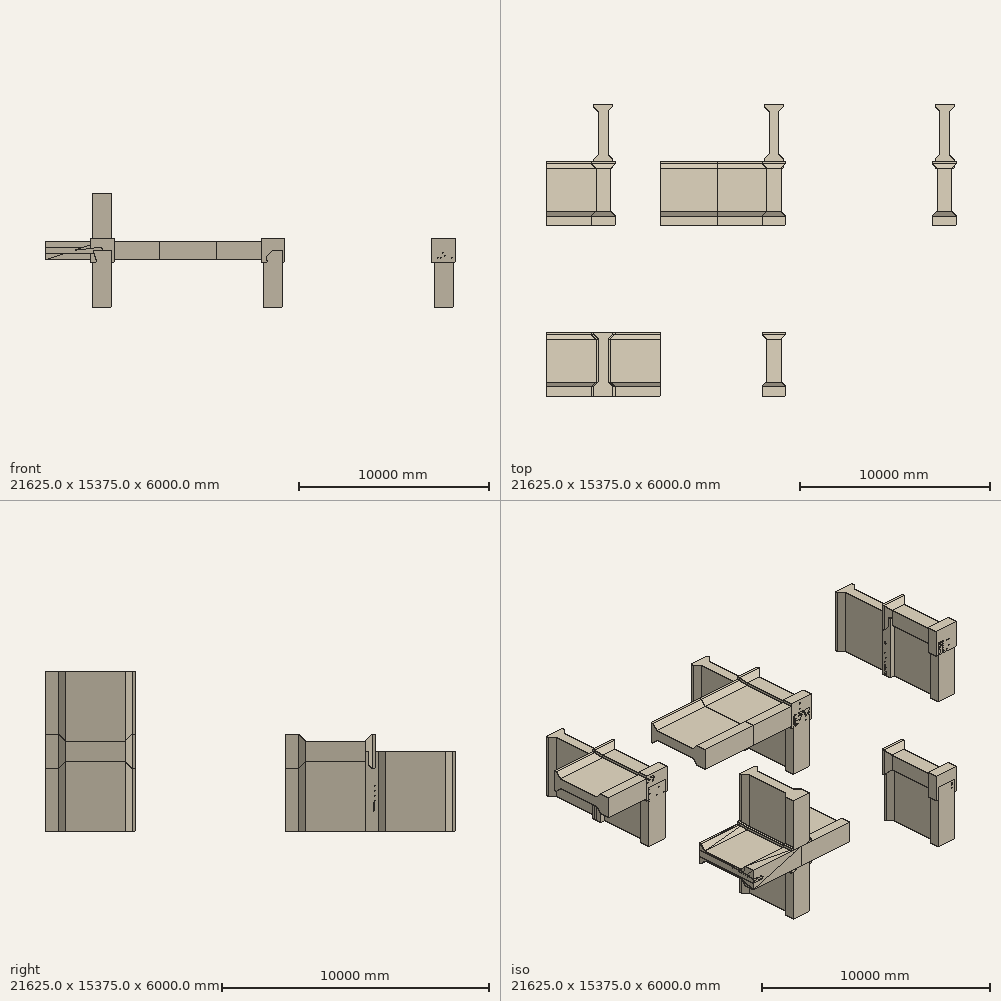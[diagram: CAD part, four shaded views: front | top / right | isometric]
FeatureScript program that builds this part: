
annotation { "Feature Type Name" : "Feature", "Feature Type Description" : "" }
export const myFeature = defineFeature(function(context is Context, id is Id, definition is map)
    precondition{}
    {
        {
            var Q0;
            Q0=qCreatedBy(makeId("Top.planeOp"),FACE);
            var sketch = newSketch(context, id + "F0", { "sketchPlane" : qUnion([Q0])});
            skLineSegment(sketch, "E0", {"start": v(-500, 0) * mm, "end": v(500, 0) * mm});
            skLineSegment(sketch, "E1", {"start": v(500, 0) * mm, "end": v(500, 500) * mm});
            skLineSegment(sketch, "E2", {"start": v(500, 500) * mm, "end": v(250, 750) * mm});
            skLineSegment(sketch, "E3", {"start": v(250, 750) * mm, "end": v(250, 3000) * mm});
            skLineSegment(sketch, "E4", {"start": v(500, 500) * mm, "end": v(250, 500) * mm, "construction": true});
            skLineSegment(sketch, "E5", {"start": v(0, 0) * mm, "end": v(0, 3375) * mm, "construction": true});
            skLineSegment(sketch, "E6", {"start": v(250, 3000) * mm, "end": v(500, 3250) * mm});
            skLineSegment(sketch, "E7", {"start": v(500, 3250) * mm, "end": v(500, 3375) * mm});
            skLineSegment(sketch, "E8", {"start": v(500, 3375) * mm, "end": v(-500, 3375) * mm});
            skLineSegment(sketch, "E9.MirrorCS", {"start": v(-500, 0) * mm, "end": v(-500, 500) * mm});
            skLineSegment(sketch, "E10.MirrorCS", {"start": v(-500, 500) * mm, "end": v(-250, 750) * mm});
            skLineSegment(sketch, "E11.MirrorCS", {"start": v(-250, 750) * mm, "end": v(-250, 3000) * mm});
            skLineSegment(sketch, "E12.MirrorCS", {"start": v(-250, 3000) * mm, "end": v(-500, 3250) * mm});
            skLineSegment(sketch, "E13.MirrorCS", {"start": v(-500, 3250) * mm, "end": v(-500, 3375) * mm});
            skLineSegment(sketch, "E14", {"start": v(-625, 0) * mm, "end": v(625, 0) * mm});
            skLineSegment(sketch, "E15", {"start": v(625, 0) * mm, "end": v(625, 500) * mm});
            skLineSegment(sketch, "E16", {"start": v(625, 500) * mm, "end": v(375, 750) * mm});
            skLineSegment(sketch, "E17", {"start": v(375, 750) * mm, "end": v(375, 3000) * mm});
            skLineSegment(sketch, "E18", {"start": v(375, 3000) * mm, "end": v(625, 3250) * mm});
            skLineSegment(sketch, "E19", {"start": v(625, 3250) * mm, "end": v(625, 3375) * mm});
            skLineSegment(sketch, "E20", {"start": v(625, 3375) * mm, "end": v(-625, 3375) * mm});
            skLineSegment(sketch, "E21.MirrorCS", {"start": v(-625, 0) * mm, "end": v(-625, 500) * mm});
            skLineSegment(sketch, "E22.MirrorCS", {"start": v(-625, 500) * mm, "end": v(-375, 750) * mm});
            skLineSegment(sketch, "E23.MirrorCS", {"start": v(-375, 750) * mm, "end": v(-375, 3000) * mm});
            skLineSegment(sketch, "E24.MirrorCS", {"start": v(-375, 3000) * mm, "end": v(-625, 3250) * mm});
            skLineSegment(sketch, "E25.MirrorCS", {"start": v(-625, 3250) * mm, "end": v(-625, 3375) * mm});
            skLineSegment(sketch, "E26", {"start": v(-625, 500) * mm, "end": v(625, 500) * mm});
            skLineSegment(sketch, "E27", {"start": v(375, 750) * mm, "end": v(-375, 750) * mm});
            skLineSegment(sketch, "E28", {"start": v(-375, 3000) * mm, "end": v(375, 3000) * mm});
            skLineSegment(sketch, "E29", {"start": v(-625, 3250) * mm, "end": v(625, 3250) * mm});
            skCircle(sketch, "E30", {"center": v(1625, 1250) * mm, "radius": 1250 * mm, "construction": true});
            skSolve(sketch);
        }
        {
            var Q0;
            {var subQ0=sQuery(id+"F0.wireOp",EDGE,"E11.MirrorCS");Q0=makeQuery(id+"F0.imprint","IMPRINT",FACE,{"disambiguationData":[TD([[makeQuery(id+"F0.imprint","IMPRINT",EDGE,{"derivedFrom":subQ0}),1.0]])]});}
            var Q1;
            {var subQ0=sQuery(id+"F0.wireOp",EDGE,"E3");Q1=makeQuery(id+"F0.imprint","IMPRINT",FACE,{"disambiguationData":[TD([[makeQuery(id+"F0.imprint","IMPRINT",EDGE,{"derivedFrom":subQ0}),-1.0]])]});}
            var Q2;
            {var subQ0=sQuery(id+"F0.wireOp",EDGE,"E3");Q2=makeQuery(id+"F0.imprint","IMPRINT",FACE,{"disambiguationData":[TD([[makeQuery(id+"F0.imprint","IMPRINT",EDGE,{"derivedFrom":subQ0}),1.0]])]});}
            extrude(context, id + "F1", {"entities" : qUnion([Q0, Q1, Q2]), "endBound" : BoundingType.SYMMETRIC, "depth" : 750 * mm, "offsetDistance" : 25 * mm});
        }
        {
            var Q0;
            {var subQ0=sQuery(id+"F0.wireOp",EDGE,"E1");Q0=makeQuery(id+"F0.imprint","IMPRINT",FACE,{"disambiguationData":[TD([[makeQuery(id+"F0.imprint","IMPRINT",EDGE,{"derivedFrom":subQ0}),-1.0]])]});}
            var Q1;
            {var subQ0=sQuery(id+"F0.wireOp",EDGE,"E2");Q1=makeQuery(id+"F0.imprint","IMPRINT",FACE,{"disambiguationData":[TD([[makeQuery(id+"F0.imprint","IMPRINT",EDGE,{"derivedFrom":subQ0}),-1.0]])]});}
            var Q2;
            {var subQ0=sQuery(id+"F0.wireOp",EDGE,"E6");Q2=makeQuery(id+"F0.imprint","IMPRINT",FACE,{"disambiguationData":[TD([[makeQuery(id+"F0.imprint","IMPRINT",EDGE,{"derivedFrom":subQ0}),-1.0]])]});}
            var Q3;
            {var subQ0=sQuery(id+"F0.wireOp",EDGE,"E7");Q3=makeQuery(id+"F0.imprint","IMPRINT",FACE,{"disambiguationData":[TD([[makeQuery(id+"F0.imprint","IMPRINT",EDGE,{"derivedFrom":subQ0}),-1.0]])]});}
            var Q4;
            {var subQ0=sQuery(id+"F0.wireOp",EDGE,"E9.MirrorCS");Q4=makeQuery(id+"F0.imprint","IMPRINT",FACE,{"disambiguationData":[TD([[makeQuery(id+"F0.imprint","IMPRINT",EDGE,{"derivedFrom":subQ0}),1.0]])]});}
            var Q5;
            {var subQ0=sQuery(id+"F0.wireOp",EDGE,"E10.MirrorCS");Q5=makeQuery(id+"F0.imprint","IMPRINT",FACE,{"disambiguationData":[TD([[makeQuery(id+"F0.imprint","IMPRINT",EDGE,{"derivedFrom":subQ0}),1.0]])]});}
            var Q6;
            {var subQ0=sQuery(id+"F0.wireOp",EDGE,"E12.MirrorCS");Q6=makeQuery(id+"F0.imprint","IMPRINT",FACE,{"disambiguationData":[TD([[makeQuery(id+"F0.imprint","IMPRINT",EDGE,{"derivedFrom":subQ0}),1.0]])]});}
            var Q7;
            {var subQ0=sQuery(id+"F0.wireOp",EDGE,"E13.MirrorCS");Q7=makeQuery(id+"F0.imprint","IMPRINT",FACE,{"disambiguationData":[TD([[makeQuery(id+"F0.imprint","IMPRINT",EDGE,{"derivedFrom":subQ0}),1.0]])]});}
            var Q8;
            {var subQ0=sQuery(id+"F0.wireOp",EDGE,"E7");Q8=makeQuery(id+"F0.imprint","IMPRINT",FACE,{"disambiguationData":[TD([[makeQuery(id+"F0.imprint","IMPRINT",EDGE,{"derivedFrom":subQ0}),1.0]])]});}
            var Q9;
            Q9=makeQuery(id+"F0.imprint","IMPRINT",FACE,{"disambiguationData":[TD([[makeQuery(id+"F0.imprint","IMPRINT",EDGE,{"derivedFrom":sQuery(id+"F0.wireOp",EDGE,"E0")}),1.0]])]});
            var Q10;
            {var subQ0=sQuery(id+"F0.wireOp",EDGE,"E2");Q10=makeQuery(id+"F0.imprint","IMPRINT",FACE,{"disambiguationData":[TD([[makeQuery(id+"F0.imprint","IMPRINT",EDGE,{"derivedFrom":subQ0}),1.0]])]});}
            var Q11;
            {var subQ0=sQuery(id+"F0.wireOp",EDGE,"E6");Q11=makeQuery(id+"F0.imprint","IMPRINT",FACE,{"disambiguationData":[TD([[makeQuery(id+"F0.imprint","IMPRINT",EDGE,{"derivedFrom":subQ0}),1.0]])]});}
            extrude(context, id + "F2", {"entities" : qUnion([Q0, Q1, Q2, Q3, Q4, Q5, Q6, Q7, Q8, Q9, Q10, Q11]), "operationType" : NewBodyOperationType.ADD, "endBound" : BoundingType.SYMMETRIC, "depth" : 1250 * mm, "offsetDistance" : 25 * mm});
        }
        {
            var Q0;
            Q0=makeQuery(id+"F2.opExtrude","CAP_EDGE",EDGE,{"disambiguationData":[OSD([sQuery(id+"F0.wireOp",EDGE,"E28")])],"isStart":false});
            var Q1;
            Q1=makeQuery(id+"F2.opExtrude","CAP_EDGE",EDGE,{"disambiguationData":[OSD([sQuery(id+"F0.wireOp",EDGE,"E28")])],"isStart":true});
            var Q2;
            Q2=makeQuery(id+"F2.opExtrude","CAP_EDGE",EDGE,{"disambiguationData":[OSD([sQuery(id+"F0.wireOp",EDGE,"E27")])],"isStart":true});
            var Q3;
            Q3=makeQuery(id+"F2.opExtrude","CAP_EDGE",EDGE,{"disambiguationData":[OSD([sQuery(id+"F0.wireOp",EDGE,"E27")])],"isStart":false});
            chamfer(context, id + "F3", {"entities" : qUnion([Q0, Q1, Q2, Q3]), "width" : 250 * mm, "tangentPropagation" : true});
        }
        {
            var Q0;
            Q0=makeQuery(id+"F0.imprint","IMPRINT",FACE,{"disambiguationData":[TD([[makeQuery(id+"F0.imprint","IMPRINT",EDGE,{"derivedFrom":sQuery(id+"F0.wireOp",EDGE,"E0")}),1.0]])]});
            var Q1;
            {var subQ0=sQuery(id+"F0.wireOp",EDGE,"E2");Q1=makeQuery(id+"F0.imprint","IMPRINT",FACE,{"disambiguationData":[TD([[makeQuery(id+"F0.imprint","IMPRINT",EDGE,{"derivedFrom":subQ0}),1.0]])]});}
            var Q2;
            {var subQ0=sQuery(id+"F0.wireOp",EDGE,"E3");Q2=makeQuery(id+"F0.imprint","IMPRINT",FACE,{"disambiguationData":[TD([[makeQuery(id+"F0.imprint","IMPRINT",EDGE,{"derivedFrom":subQ0}),1.0]])]});}
            var Q3;
            {var subQ0=sQuery(id+"F0.wireOp",EDGE,"E3");Q3=makeQuery(id+"F0.imprint","IMPRINT",FACE,{"disambiguationData":[TD([[makeQuery(id+"F0.imprint","IMPRINT",EDGE,{"derivedFrom":subQ0}),1.0]])]});}
            var Q4;
            {var subQ0=sQuery(id+"F0.wireOp",EDGE,"E7");Q4=makeQuery(id+"F0.imprint","IMPRINT",FACE,{"disambiguationData":[TD([[makeQuery(id+"F0.imprint","IMPRINT",EDGE,{"derivedFrom":subQ0}),1.0]])]});}
            var Q5;
            {var subQ0=sQuery(id+"F0.wireOp",EDGE,"E6");Q5=makeQuery(id+"F0.imprint","IMPRINT",FACE,{"disambiguationData":[TD([[makeQuery(id+"F0.imprint","IMPRINT",EDGE,{"derivedFrom":subQ0}),1.0]])]});}
            extrude(context, id + "F4", {"entities" : qUnion([Q0, Q1, Q2, Q3, Q4, Q5]), "oppositeDirection" : true, "depth" : 3000 * mm, "offsetDistance" : 25 * mm});
        }
        {
            var Q0;
            Q0=makeQuery(id+"F4.opExtrude","SWEPT_BODY",BODY,{"disambiguationData":[OSD([sQuery(id+"F0.wireOp",EDGE,"E0"),sQuery(id+"F0.wireOp",EDGE,"E1"),sQuery(id+"F0.wireOp",EDGE,"E2"),sQuery(id+"F0.wireOp",EDGE,"E3"),sQuery(id+"F0.wireOp",EDGE,"E6"),sQuery(id+"F0.wireOp",EDGE,"E7"),sQuery(id+"F0.wireOp",EDGE,"E8"),sQuery(id+"F0.wireOp",EDGE,"E9.MirrorCS"),sQuery(id+"F0.wireOp",EDGE,"E10.MirrorCS"),sQuery(id+"F0.wireOp",EDGE,"E11.MirrorCS"),sQuery(id+"F0.wireOp",EDGE,"E12.MirrorCS"),sQuery(id+"F0.wireOp",EDGE,"E13.MirrorCS")])]});
            var Q1;
            Q1=sQuery(id+"F0.wireOp",EDGE,"E5");
            transform(context, id + "F5", {"entities" : qUnion([Q0]), "transformType" : TransformType.ROTATION, "transformAxis" : qUnion([Q1]), "angle" : 90 * degree, "makeCopy" : true});
        }
        {
            var Q0;
            Q0=makeQuery(id+"F5.opPattern","COPY",BODY,{"derivedFrom":makeQuery(id+"F4.opExtrude","SWEPT_BODY",BODY,{"disambiguationData":[OSD([sQuery(id+"F0.wireOp",EDGE,"E0"),sQuery(id+"F0.wireOp",EDGE,"E1"),sQuery(id+"F0.wireOp",EDGE,"E2"),sQuery(id+"F0.wireOp",EDGE,"E3"),sQuery(id+"F0.wireOp",EDGE,"E6"),sQuery(id+"F0.wireOp",EDGE,"E7"),sQuery(id+"F0.wireOp",EDGE,"E8"),sQuery(id+"F0.wireOp",EDGE,"E9.MirrorCS"),sQuery(id+"F0.wireOp",EDGE,"E10.MirrorCS"),sQuery(id+"F0.wireOp",EDGE,"E11.MirrorCS"),sQuery(id+"F0.wireOp",EDGE,"E12.MirrorCS"),sQuery(id+"F0.wireOp",EDGE,"E13.MirrorCS")])]}),"instanceName":"1"});
            var Q1;
            Q1=makeQuery(id+"F4.opExtrude","SWEPT_BODY",BODY,{"disambiguationData":[OSD([sQuery(id+"F0.wireOp",EDGE,"E0"),sQuery(id+"F0.wireOp",EDGE,"E1"),sQuery(id+"F0.wireOp",EDGE,"E2"),sQuery(id+"F0.wireOp",EDGE,"E3"),sQuery(id+"F0.wireOp",EDGE,"E6"),sQuery(id+"F0.wireOp",EDGE,"E7"),sQuery(id+"F0.wireOp",EDGE,"E8"),sQuery(id+"F0.wireOp",EDGE,"E9.MirrorCS"),sQuery(id+"F0.wireOp",EDGE,"E10.MirrorCS"),sQuery(id+"F0.wireOp",EDGE,"E11.MirrorCS"),sQuery(id+"F0.wireOp",EDGE,"E12.MirrorCS"),sQuery(id+"F0.wireOp",EDGE,"E13.MirrorCS")])]});
            var Q2;
            Q2=sQuery(id+"F0.wireOp",EDGE,"E5");
            transform(context, id + "F6", {"entities" : qUnion([Q0, Q1]), "transformType" : TransformType.ROTATION, "transformAxis" : qUnion([Q2]), "angle" : 180 * degree, "makeCopy" : true});
        }
        {
            var Q0;
            Q0=makeQuery(id+"F4.opExtrude","SWEPT_BODY",BODY,{"disambiguationData":[OSD([sQuery(id+"F0.wireOp",EDGE,"E1"),sQuery(id+"F0.wireOp",EDGE,"E2"),sQuery(id+"F0.wireOp",EDGE,"E3"),sQuery(id+"F0.wireOp",EDGE,"E6"),sQuery(id+"F0.wireOp",EDGE,"E7"),sQuery(id+"F0.wireOp",EDGE,"E9.MirrorCS"),sQuery(id+"F0.wireOp",EDGE,"E10.MirrorCS"),sQuery(id+"F0.wireOp",EDGE,"E11.MirrorCS"),sQuery(id+"F0.wireOp",EDGE,"E12.MirrorCS"),sQuery(id+"F0.wireOp",EDGE,"E13.MirrorCS"),sQuery(id+"F0.wireOp",EDGE,"E14"),sQuery(id+"F0.wireOp",EDGE,"E20")])]});
            var Q1;
            Q1=makeQuery(id+"F1.opExtrude","SWEPT_BODY",BODY,{"disambiguationData":[OSD([sQuery(id+"F0.wireOp",EDGE,"E17"),sQuery(id+"F0.wireOp",EDGE,"E23.MirrorCS"),sQuery(id+"F0.wireOp",EDGE,"E27"),sQuery(id+"F0.wireOp",EDGE,"E28")])]});
            transform(context, id + "F7", {"entities" : qUnion([Q0, Q1]), "transformType" : TransformType.TRANSLATION_3D, "dx" : 0 * mm, "dy" : 9000 * mm, "dz" : 0 * mm, "makeCopy" : true});
        }
        {
            var Q0;
            Q0=makeQuery(id+"F7.opPattern","COPY",BODY,{"derivedFrom":makeQuery(id+"F4.opExtrude","SWEPT_BODY",BODY,{"disambiguationData":[OSD([sQuery(id+"F0.wireOp",EDGE,"E1"),sQuery(id+"F0.wireOp",EDGE,"E2"),sQuery(id+"F0.wireOp",EDGE,"E3"),sQuery(id+"F0.wireOp",EDGE,"E6"),sQuery(id+"F0.wireOp",EDGE,"E7"),sQuery(id+"F0.wireOp",EDGE,"E9.MirrorCS"),sQuery(id+"F0.wireOp",EDGE,"E10.MirrorCS"),sQuery(id+"F0.wireOp",EDGE,"E11.MirrorCS"),sQuery(id+"F0.wireOp",EDGE,"E12.MirrorCS"),sQuery(id+"F0.wireOp",EDGE,"E13.MirrorCS"),sQuery(id+"F0.wireOp",EDGE,"E14"),sQuery(id+"F0.wireOp",EDGE,"E20")])]}),"instanceName":"1"});
            var Q1;
            Q1=makeQuery(id+"F7.opPattern","COPY",BODY,{"derivedFrom":makeQuery(id+"F1.opExtrude","SWEPT_BODY",BODY,{"disambiguationData":[OSD([sQuery(id+"F0.wireOp",EDGE,"E17"),sQuery(id+"F0.wireOp",EDGE,"E23.MirrorCS"),sQuery(id+"F0.wireOp",EDGE,"E27"),sQuery(id+"F0.wireOp",EDGE,"E28")])]}),"instanceName":"1"});
            var Q2;
            Q2=makeQuery(id+"F1.opExtrude","SWEPT_BODY",BODY,{"disambiguationData":[OSD([sQuery(id+"F0.wireOp",EDGE,"E17"),sQuery(id+"F0.wireOp",EDGE,"E23.MirrorCS"),sQuery(id+"F0.wireOp",EDGE,"E27"),sQuery(id+"F0.wireOp",EDGE,"E28")])]});
            var Q3;
            Q3=makeQuery(id+"F4.opExtrude","SWEPT_BODY",BODY,{"disambiguationData":[OSD([sQuery(id+"F0.wireOp",EDGE,"E1"),sQuery(id+"F0.wireOp",EDGE,"E2"),sQuery(id+"F0.wireOp",EDGE,"E3"),sQuery(id+"F0.wireOp",EDGE,"E6"),sQuery(id+"F0.wireOp",EDGE,"E7"),sQuery(id+"F0.wireOp",EDGE,"E9.MirrorCS"),sQuery(id+"F0.wireOp",EDGE,"E10.MirrorCS"),sQuery(id+"F0.wireOp",EDGE,"E11.MirrorCS"),sQuery(id+"F0.wireOp",EDGE,"E12.MirrorCS"),sQuery(id+"F0.wireOp",EDGE,"E13.MirrorCS"),sQuery(id+"F0.wireOp",EDGE,"E14"),sQuery(id+"F0.wireOp",EDGE,"E20")])]});
            transform(context, id + "F8", {"entities" : qUnion([Q0, Q1, Q2, Q3]), "transformType" : TransformType.TRANSLATION_3D, "dx" : 9000 * mm, "dy" : 0 * mm, "dz" : 0 * mm, "makeCopy" : true});
        }
        {
            var Q0;
            Q0=makeQuery(id+"F8.opPattern","COPY",BODY,{"derivedFrom":makeQuery(id+"F7.opPattern","COPY",BODY,{"derivedFrom":makeQuery(id+"F1.opExtrude","SWEPT_BODY",BODY,{"disambiguationData":[OSD([sQuery(id+"F0.wireOp",EDGE,"E17"),sQuery(id+"F0.wireOp",EDGE,"E23.MirrorCS"),sQuery(id+"F0.wireOp",EDGE,"E27"),sQuery(id+"F0.wireOp",EDGE,"E28")])]}),"instanceName":"1"}),"instanceName":"1"});
            var Q1;
            Q1=makeQuery(id+"F8.opPattern","COPY",BODY,{"derivedFrom":makeQuery(id+"F7.opPattern","COPY",BODY,{"derivedFrom":makeQuery(id+"F4.opExtrude","SWEPT_BODY",BODY,{"disambiguationData":[OSD([sQuery(id+"F0.wireOp",EDGE,"E1"),sQuery(id+"F0.wireOp",EDGE,"E2"),sQuery(id+"F0.wireOp",EDGE,"E3"),sQuery(id+"F0.wireOp",EDGE,"E6"),sQuery(id+"F0.wireOp",EDGE,"E7"),sQuery(id+"F0.wireOp",EDGE,"E9.MirrorCS"),sQuery(id+"F0.wireOp",EDGE,"E10.MirrorCS"),sQuery(id+"F0.wireOp",EDGE,"E11.MirrorCS"),sQuery(id+"F0.wireOp",EDGE,"E12.MirrorCS"),sQuery(id+"F0.wireOp",EDGE,"E13.MirrorCS"),sQuery(id+"F0.wireOp",EDGE,"E14"),sQuery(id+"F0.wireOp",EDGE,"E20")])]}),"instanceName":"1"}),"instanceName":"1"});
            var Q2;
            Q2=makeQuery(id+"F8.opPattern","COPY",BODY,{"derivedFrom":makeQuery(id+"F1.opExtrude","SWEPT_BODY",BODY,{"disambiguationData":[OSD([sQuery(id+"F0.wireOp",EDGE,"E17"),sQuery(id+"F0.wireOp",EDGE,"E23.MirrorCS"),sQuery(id+"F0.wireOp",EDGE,"E27"),sQuery(id+"F0.wireOp",EDGE,"E28")])]}),"instanceName":"1"});
            var Q3;
            Q3=makeQuery(id+"F8.opPattern","COPY",BODY,{"derivedFrom":makeQuery(id+"F4.opExtrude","SWEPT_BODY",BODY,{"disambiguationData":[OSD([sQuery(id+"F0.wireOp",EDGE,"E1"),sQuery(id+"F0.wireOp",EDGE,"E2"),sQuery(id+"F0.wireOp",EDGE,"E3"),sQuery(id+"F0.wireOp",EDGE,"E6"),sQuery(id+"F0.wireOp",EDGE,"E7"),sQuery(id+"F0.wireOp",EDGE,"E9.MirrorCS"),sQuery(id+"F0.wireOp",EDGE,"E10.MirrorCS"),sQuery(id+"F0.wireOp",EDGE,"E11.MirrorCS"),sQuery(id+"F0.wireOp",EDGE,"E12.MirrorCS"),sQuery(id+"F0.wireOp",EDGE,"E13.MirrorCS"),sQuery(id+"F0.wireOp",EDGE,"E14"),sQuery(id+"F0.wireOp",EDGE,"E20")])]}),"instanceName":"1"});
            transform(context, id + "F9", {"entities" : qUnion([Q0, Q1, Q2, Q3]), "transformType" : TransformType.TRANSLATION_3D, "dx" : 9000 * mm, "dy" : 0 * mm, "dz" : 0 * mm, "makeCopy" : true});
        }
        {
            var Q0;
            Q0=makeQuery(id+"F7.opPattern","COPY",BODY,{"derivedFrom":makeQuery(id+"F4.opExtrude","SWEPT_BODY",BODY,{"disambiguationData":[OSD([sQuery(id+"F0.wireOp",EDGE,"E1"),sQuery(id+"F0.wireOp",EDGE,"E2"),sQuery(id+"F0.wireOp",EDGE,"E3"),sQuery(id+"F0.wireOp",EDGE,"E6"),sQuery(id+"F0.wireOp",EDGE,"E7"),sQuery(id+"F0.wireOp",EDGE,"E9.MirrorCS"),sQuery(id+"F0.wireOp",EDGE,"E10.MirrorCS"),sQuery(id+"F0.wireOp",EDGE,"E11.MirrorCS"),sQuery(id+"F0.wireOp",EDGE,"E12.MirrorCS"),sQuery(id+"F0.wireOp",EDGE,"E13.MirrorCS"),sQuery(id+"F0.wireOp",EDGE,"E14"),sQuery(id+"F0.wireOp",EDGE,"E20")])]}),"instanceName":"1"});
            var Q1;
            Q1=makeQuery(id+"F8.opPattern","COPY",BODY,{"derivedFrom":makeQuery(id+"F7.opPattern","COPY",BODY,{"derivedFrom":makeQuery(id+"F4.opExtrude","SWEPT_BODY",BODY,{"disambiguationData":[OSD([sQuery(id+"F0.wireOp",EDGE,"E1"),sQuery(id+"F0.wireOp",EDGE,"E2"),sQuery(id+"F0.wireOp",EDGE,"E3"),sQuery(id+"F0.wireOp",EDGE,"E6"),sQuery(id+"F0.wireOp",EDGE,"E7"),sQuery(id+"F0.wireOp",EDGE,"E9.MirrorCS"),sQuery(id+"F0.wireOp",EDGE,"E10.MirrorCS"),sQuery(id+"F0.wireOp",EDGE,"E11.MirrorCS"),sQuery(id+"F0.wireOp",EDGE,"E12.MirrorCS"),sQuery(id+"F0.wireOp",EDGE,"E13.MirrorCS"),sQuery(id+"F0.wireOp",EDGE,"E14"),sQuery(id+"F0.wireOp",EDGE,"E20")])]}),"instanceName":"1"}),"instanceName":"1"});
            var Q2;
            Q2=makeQuery(id+"F9.opPattern","COPY",BODY,{"derivedFrom":makeQuery(id+"F8.opPattern","COPY",BODY,{"derivedFrom":makeQuery(id+"F7.opPattern","COPY",BODY,{"derivedFrom":makeQuery(id+"F4.opExtrude","SWEPT_BODY",BODY,{"disambiguationData":[OSD([sQuery(id+"F0.wireOp",EDGE,"E1"),sQuery(id+"F0.wireOp",EDGE,"E2"),sQuery(id+"F0.wireOp",EDGE,"E3"),sQuery(id+"F0.wireOp",EDGE,"E6"),sQuery(id+"F0.wireOp",EDGE,"E7"),sQuery(id+"F0.wireOp",EDGE,"E9.MirrorCS"),sQuery(id+"F0.wireOp",EDGE,"E10.MirrorCS"),sQuery(id+"F0.wireOp",EDGE,"E11.MirrorCS"),sQuery(id+"F0.wireOp",EDGE,"E12.MirrorCS"),sQuery(id+"F0.wireOp",EDGE,"E13.MirrorCS"),sQuery(id+"F0.wireOp",EDGE,"E14"),sQuery(id+"F0.wireOp",EDGE,"E20")])]}),"instanceName":"1"}),"instanceName":"1"}),"instanceName":"1"});
            var Q3;
            Q3=makeQuery(id+"F9.opPattern","COPY",BODY,{"derivedFrom":makeQuery(id+"F8.opPattern","COPY",BODY,{"derivedFrom":makeQuery(id+"F4.opExtrude","SWEPT_BODY",BODY,{"disambiguationData":[OSD([sQuery(id+"F0.wireOp",EDGE,"E1"),sQuery(id+"F0.wireOp",EDGE,"E2"),sQuery(id+"F0.wireOp",EDGE,"E3"),sQuery(id+"F0.wireOp",EDGE,"E6"),sQuery(id+"F0.wireOp",EDGE,"E7"),sQuery(id+"F0.wireOp",EDGE,"E9.MirrorCS"),sQuery(id+"F0.wireOp",EDGE,"E10.MirrorCS"),sQuery(id+"F0.wireOp",EDGE,"E11.MirrorCS"),sQuery(id+"F0.wireOp",EDGE,"E12.MirrorCS"),sQuery(id+"F0.wireOp",EDGE,"E13.MirrorCS"),sQuery(id+"F0.wireOp",EDGE,"E14"),sQuery(id+"F0.wireOp",EDGE,"E20")])]}),"instanceName":"1"}),"instanceName":"1"});
            transform(context, id + "F10", {"entities" : qUnion([Q0, Q1, Q2, Q3]), "transformType" : TransformType.TRANSLATION_3D, "dx" : 0 * mm, "dy" : 3000 * mm, "dz" : 0 * mm, "makeCopy" : true});
        }
        {
            var Q0;
            Q0=makeQuery(id+"F4.opExtrude","SWEPT_BODY",BODY,{"disambiguationData":[OSD([sQuery(id+"F0.wireOp",EDGE,"E1"),sQuery(id+"F0.wireOp",EDGE,"E2"),sQuery(id+"F0.wireOp",EDGE,"E3"),sQuery(id+"F0.wireOp",EDGE,"E6"),sQuery(id+"F0.wireOp",EDGE,"E7"),sQuery(id+"F0.wireOp",EDGE,"E9.MirrorCS"),sQuery(id+"F0.wireOp",EDGE,"E10.MirrorCS"),sQuery(id+"F0.wireOp",EDGE,"E11.MirrorCS"),sQuery(id+"F0.wireOp",EDGE,"E12.MirrorCS"),sQuery(id+"F0.wireOp",EDGE,"E13.MirrorCS"),sQuery(id+"F0.wireOp",EDGE,"E14"),sQuery(id+"F0.wireOp",EDGE,"E20")])]});
            var Q1;
            Q1=sQuery(id+"F0.wireOp",EDGE,"E5");
            transform(context, id + "F11", {"entities" : qUnion([Q0]), "transformType" : TransformType.ROTATION, "transformAxis" : qUnion([Q1]), "angle" : 90 * degree, "makeCopy" : true});
        }
        {
            var Q0;
            Q0=makeQuery(id+"F11.opPattern","COPY",BODY,{"derivedFrom":makeQuery(id+"F4.opExtrude","SWEPT_BODY",BODY,{"disambiguationData":[OSD([sQuery(id+"F0.wireOp",EDGE,"E1"),sQuery(id+"F0.wireOp",EDGE,"E2"),sQuery(id+"F0.wireOp",EDGE,"E3"),sQuery(id+"F0.wireOp",EDGE,"E6"),sQuery(id+"F0.wireOp",EDGE,"E7"),sQuery(id+"F0.wireOp",EDGE,"E9.MirrorCS"),sQuery(id+"F0.wireOp",EDGE,"E10.MirrorCS"),sQuery(id+"F0.wireOp",EDGE,"E11.MirrorCS"),sQuery(id+"F0.wireOp",EDGE,"E12.MirrorCS"),sQuery(id+"F0.wireOp",EDGE,"E13.MirrorCS"),sQuery(id+"F0.wireOp",EDGE,"E14"),sQuery(id+"F0.wireOp",EDGE,"E20")])]}),"instanceName":"1"});
            transform(context, id + "F12", {"entities" : qUnion([Q0]), "transformType" : TransformType.TRANSLATION_3D, "dx" : 0 * mm, "dy" : 9000 * mm, "dz" : 0 * mm, "makeCopy" : true});
        }
        {
            var Q0;
            Q0=makeQuery(id+"F12.opPattern","COPY",BODY,{"derivedFrom":makeQuery(id+"F11.opPattern","COPY",BODY,{"derivedFrom":makeQuery(id+"F4.opExtrude","SWEPT_BODY",BODY,{"disambiguationData":[OSD([sQuery(id+"F0.wireOp",EDGE,"E1"),sQuery(id+"F0.wireOp",EDGE,"E2"),sQuery(id+"F0.wireOp",EDGE,"E3"),sQuery(id+"F0.wireOp",EDGE,"E6"),sQuery(id+"F0.wireOp",EDGE,"E7"),sQuery(id+"F0.wireOp",EDGE,"E9.MirrorCS"),sQuery(id+"F0.wireOp",EDGE,"E10.MirrorCS"),sQuery(id+"F0.wireOp",EDGE,"E11.MirrorCS"),sQuery(id+"F0.wireOp",EDGE,"E12.MirrorCS"),sQuery(id+"F0.wireOp",EDGE,"E13.MirrorCS"),sQuery(id+"F0.wireOp",EDGE,"E14"),sQuery(id+"F0.wireOp",EDGE,"E20")])]}),"instanceName":"1"}),"instanceName":"1"});
            transform(context, id + "F13", {"entities" : qUnion([Q0]), "transformType" : TransformType.TRANSLATION_3D, "dx" : 9000 * mm, "dy" : 0 * mm, "dz" : 0 * mm, "makeCopy" : true});
        }
        {
            var Q0;
            Q0=makeQuery(id+"F13.opPattern","COPY",BODY,{"derivedFrom":makeQuery(id+"F12.opPattern","COPY",BODY,{"derivedFrom":makeQuery(id+"F11.opPattern","COPY",BODY,{"derivedFrom":makeQuery(id+"F4.opExtrude","SWEPT_BODY",BODY,{"disambiguationData":[OSD([sQuery(id+"F0.wireOp",EDGE,"E1"),sQuery(id+"F0.wireOp",EDGE,"E2"),sQuery(id+"F0.wireOp",EDGE,"E3"),sQuery(id+"F0.wireOp",EDGE,"E6"),sQuery(id+"F0.wireOp",EDGE,"E7"),sQuery(id+"F0.wireOp",EDGE,"E9.MirrorCS"),sQuery(id+"F0.wireOp",EDGE,"E10.MirrorCS"),sQuery(id+"F0.wireOp",EDGE,"E11.MirrorCS"),sQuery(id+"F0.wireOp",EDGE,"E12.MirrorCS"),sQuery(id+"F0.wireOp",EDGE,"E13.MirrorCS"),sQuery(id+"F0.wireOp",EDGE,"E14"),sQuery(id+"F0.wireOp",EDGE,"E20")])]}),"instanceName":"1"}),"instanceName":"1"}),"instanceName":"1"});
            transform(context, id + "F14", {"entities" : qUnion([Q0]), "transformType" : TransformType.TRANSLATION_3D, "dx" : -3000 * mm, "dy" : 0 * mm, "dz" : 0 * mm, "makeCopy" : true});
        }
        {
            var Q0;
            Q0=makeQuery(id+"F10.opPattern","COPY",BODY,{"derivedFrom":makeQuery(id+"F9.opPattern","COPY",BODY,{"derivedFrom":makeQuery(id+"F8.opPattern","COPY",BODY,{"derivedFrom":makeQuery(id+"F4.opExtrude","SWEPT_BODY",BODY,{"disambiguationData":[OSD([sQuery(id+"F0.wireOp",EDGE,"E1"),sQuery(id+"F0.wireOp",EDGE,"E2"),sQuery(id+"F0.wireOp",EDGE,"E3"),sQuery(id+"F0.wireOp",EDGE,"E6"),sQuery(id+"F0.wireOp",EDGE,"E7"),sQuery(id+"F0.wireOp",EDGE,"E9.MirrorCS"),sQuery(id+"F0.wireOp",EDGE,"E10.MirrorCS"),sQuery(id+"F0.wireOp",EDGE,"E11.MirrorCS"),sQuery(id+"F0.wireOp",EDGE,"E12.MirrorCS"),sQuery(id+"F0.wireOp",EDGE,"E13.MirrorCS"),sQuery(id+"F0.wireOp",EDGE,"E14"),sQuery(id+"F0.wireOp",EDGE,"E20")])]}),"instanceName":"1"}),"instanceName":"1"}),"instanceName":"1"});
            var Q1;
            Q1=makeQuery(id+"F9.opPattern","COPY",BODY,{"derivedFrom":makeQuery(id+"F8.opPattern","COPY",BODY,{"derivedFrom":makeQuery(id+"F4.opExtrude","SWEPT_BODY",BODY,{"disambiguationData":[OSD([sQuery(id+"F0.wireOp",EDGE,"E1"),sQuery(id+"F0.wireOp",EDGE,"E2"),sQuery(id+"F0.wireOp",EDGE,"E3"),sQuery(id+"F0.wireOp",EDGE,"E6"),sQuery(id+"F0.wireOp",EDGE,"E7"),sQuery(id+"F0.wireOp",EDGE,"E9.MirrorCS"),sQuery(id+"F0.wireOp",EDGE,"E10.MirrorCS"),sQuery(id+"F0.wireOp",EDGE,"E11.MirrorCS"),sQuery(id+"F0.wireOp",EDGE,"E12.MirrorCS"),sQuery(id+"F0.wireOp",EDGE,"E13.MirrorCS"),sQuery(id+"F0.wireOp",EDGE,"E14"),sQuery(id+"F0.wireOp",EDGE,"E20")])]}),"instanceName":"1"}),"instanceName":"1"});
            var Q2;
            Q2=makeQuery(id+"F9.opPattern","COPY",BODY,{"derivedFrom":makeQuery(id+"F8.opPattern","COPY",BODY,{"derivedFrom":makeQuery(id+"F1.opExtrude","SWEPT_BODY",BODY,{"disambiguationData":[OSD([sQuery(id+"F0.wireOp",EDGE,"E17"),sQuery(id+"F0.wireOp",EDGE,"E23.MirrorCS"),sQuery(id+"F0.wireOp",EDGE,"E27"),sQuery(id+"F0.wireOp",EDGE,"E28")])]}),"instanceName":"1"}),"instanceName":"1"});
            deleteBodies(context, id + "F15", {"entities" : qUnion([Q0, Q1, Q2])});
        }
        {
            var Q0;
            Q0=qCreatedBy(makeId("Front.planeOp"),FACE);
            var sketch = newSketch(context, id + "F16", { "sketchPlane" : qUnion([Q0])});
            skLineSegment(sketch, "E31", {"start": v(-3000, 166.67) * mm, "end": v(-3000, -166.67) * mm});
            skLineSegment(sketch, "E32", {"start": v(-3000, -166.67) * mm, "end": v(-97.63, -166.67) * mm});
            skLineSegment(sketch, "E33", {"start": v(-97.63, -166.67) * mm, "end": v(0, -69.04) * mm});
            skLineSegment(sketch, "E34", {"start": v(0, -69.04) * mm, "end": v(0, 69.04) * mm});
            skLineSegment(sketch, "E35", {"start": v(0, 69.04) * mm, "end": v(-97.63, 166.67) * mm});
            skLineSegment(sketch, "E36", {"start": v(-97.63, 166.67) * mm, "end": v(-3000, 166.67) * mm});
            skLineSegment(sketch, "E37", {"start": v(-3000, 0) * mm, "end": v(0, 0) * mm, "construction": true});
            skSolve(sketch);
        }
        {
            var Q0;
            Q0=makeQuery(id+"F16.imprint","IMPRINT",FACE,{"disambiguationData":[TD([[makeQuery(id+"F16.imprint","IMPRINT",EDGE,{"derivedFrom":sQuery(id+"F16.wireOp",EDGE,"E31")}),1.0]])]});
            extrude(context, id + "F17", {"entities" : qUnion([Q0]), "oppositeDirection" : true, "depth" : 3375 * mm, "offsetDistance" : 25 * mm});
        }
    });
